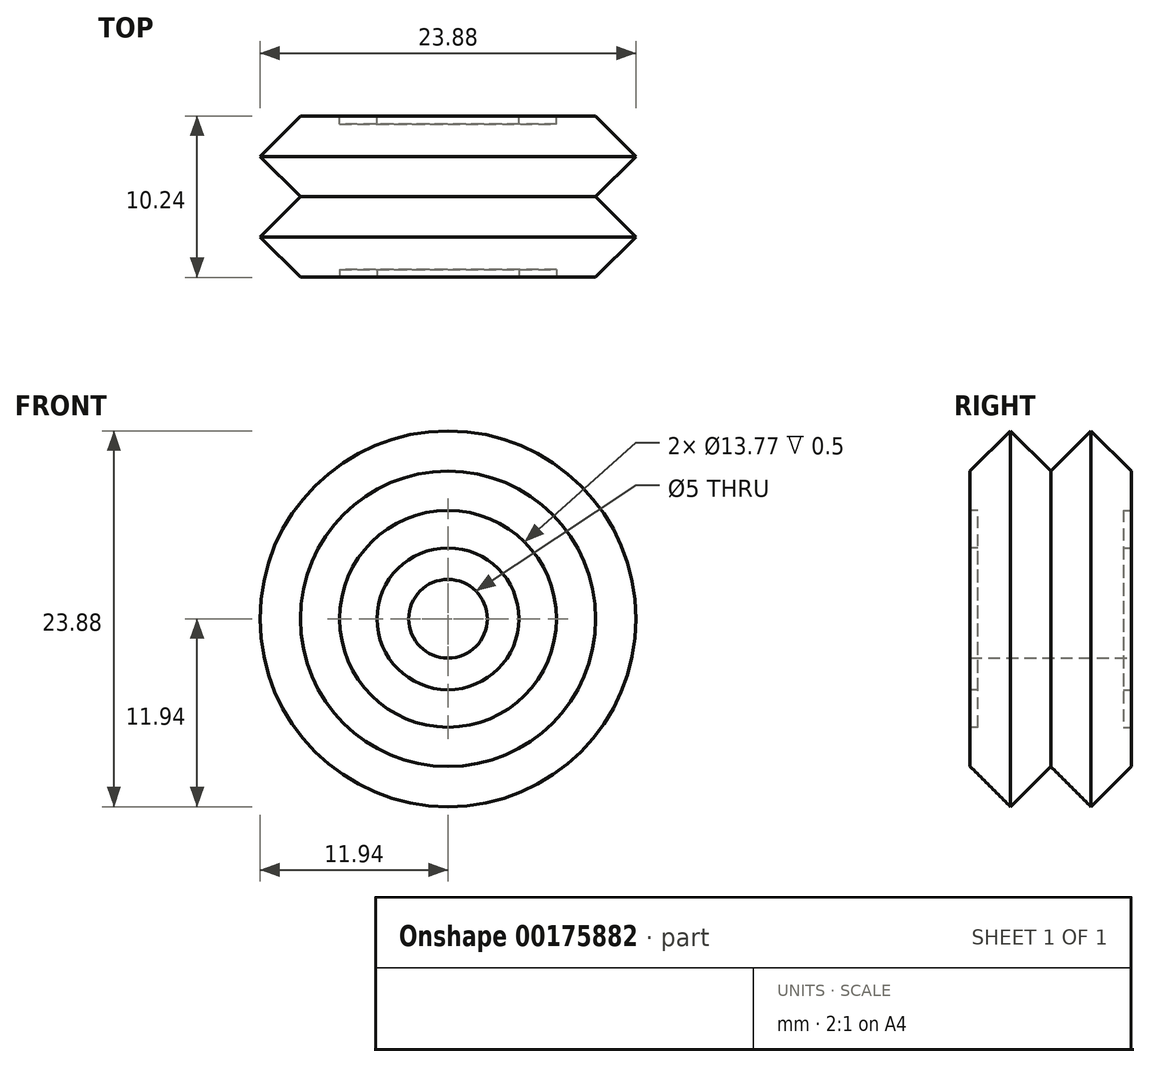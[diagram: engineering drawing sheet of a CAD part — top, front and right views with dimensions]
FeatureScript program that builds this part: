
annotation { "Feature Type Name" : "Feature", "Feature Type Description" : "" }
export const myFeature = defineFeature(function(context is Context, id is Id, definition is map)
    precondition{}
    {
        {
            var Q0;
            Q0=qCreatedBy(makeId("Front.planeOp"),FACE);
            var sketch = newSketch(context, id + "F0", { "sketchPlane" : qUnion([Q0])});
            skCircle(sketch, "E0", {"center": v(0, 0) * mm, "radius": 9.38 * mm});
            skCircle(sketch, "E1", {"center": v(0, 0) * mm, "radius": 2.5 * mm});
            skSolve(sketch);
        }
        {
            var Q0;
            Q0 = qSketchRegion(id + "F0", true);
            extrude(context, id + "F1", {"entities" : qUnion([Q0]), "endBound" : BoundingType.SYMMETRIC, "depth" : 10.23 * mm});
        }
        {
            var Q0;
            Q0=qCreatedBy(makeId("Right.planeOp"),FACE);
            var sketch = newSketch(context, id + "F2", { "sketchPlane" : qUnion([Q0])});
            skLineSegment(sketch, "E2", {"start": v(0, 9.38) * mm, "end": v(-2.56, 11.94) * mm});
            skLineSegment(sketch, "E3.0", {"start": v(0, -9.38) * mm, "end": v(0, 9.38) * mm, "construction": true});
            skLineSegment(sketch, "E4", {"start": v(0, 9.38) * mm, "end": v(2.56, 11.94) * mm});
            skLineSegment(sketch, "E5", {"start": v(-2.56, 11.94) * mm, "end": v(-5.11, 9.38) * mm});
            skLineSegment(sketch, "E6", {"start": v(-5.12, 9.38) * mm, "end": v(0, 9.38) * mm});
            skLineSegment(sketch, "E7", {"start": v(2.56, 11.94) * mm, "end": v(5.12, 9.38) * mm});
            skLineSegment(sketch, "E8", {"start": v(5.12, 9.38) * mm, "end": v(0, 9.38) * mm});
            skLineSegment(sketch, "E9", {"start": v(-5.12, 0) * mm, "end": v(5.12, 0) * mm, "construction": true});
            skCircle(sketch, "E10", {"center": v(0, 16.23) * mm, "radius": 5 * mm});
            skSolve(sketch);
        }
        {
            var Q0;
            Q0=makeQuery(id+"F2.imprint","IMPRINT",FACE,{"disambiguationData":[TD([[makeQuery(id+"F2.imprint","IMPRINT",EDGE,{"derivedFrom":sQuery(id+"F2.wireOp",EDGE,"E2")}),1.0]])]});
            var Q1;
            Q1=makeQuery(id+"F2.imprint","IMPRINT",FACE,{"disambiguationData":[TD([[makeQuery(id+"F2.imprint","IMPRINT",EDGE,{"derivedFrom":sQuery(id+"F2.wireOp",EDGE,"E4")}),-1.0]])]});
            var Q2;
            Q2=sQuery(id+"F2.wireOp",EDGE,"E9");
            revolve(context, id + "F3", {"operationType" : NewBodyOperationType.ADD, "entities" : qUnion([Q0, Q1]), "axis" : qUnion([Q2]), "revolveType" : RevolveType.FULL});
        }
        {
            var Q0;
            Q0=makeQuery(id+"F1.opExtrude","CAP_FACE",FACE,{"disambiguationData":[OSD([sQuery(id+"F0.wireOp",EDGE,"E0"),sQuery(id+"F0.wireOp",EDGE,"E1")])],"isStart":false});
            var sketch = newSketch(context, id + "F4", { "sketchPlane" : qUnion([Q0])});
            skCircle(sketch, "E11", {"center": v(0, 0) * mm, "radius": 4.5 * mm});
            skCircle(sketch, "E12", {"center": v(0, 0) * mm, "radius": 6.88 * mm});
            skSolve(sketch);
        }
        {
            var Q0;
            Q0 = qSketchRegion(id + "F4", true);
            extrude(context, id + "F5", {"entities" : qUnion([Q0]), "operationType" : NewBodyOperationType.REMOVE, "oppositeDirection" : true, "depth" : 0.5 * mm});
        }
        {
            var Q0;
            Q0=makeQuery(id+"F1.opExtrude","CAP_FACE",FACE,{"disambiguationData":[OSD([sQuery(id+"F0.wireOp",EDGE,"E0"),sQuery(id+"F0.wireOp",EDGE,"E1")])],"isStart":true});
            var sketch = newSketch(context, id + "F6", { "sketchPlane" : qUnion([Q0])});
            skCircle(sketch, "E13.0", {"center": v(0, 0) * mm, "radius": 4.5 * mm});
            skCircle(sketch, "E14.0", {"center": v(0, 0) * mm, "radius": 6.88 * mm});
            skSolve(sketch);
        }
        {
            var Q0;
            Q0 = qSketchRegion(id + "F6", true);
            extrude(context, id + "F7", {"entities" : qUnion([Q0]), "operationType" : NewBodyOperationType.REMOVE, "oppositeDirection" : true, "depth" : 0.5 * mm});
        }
    });
